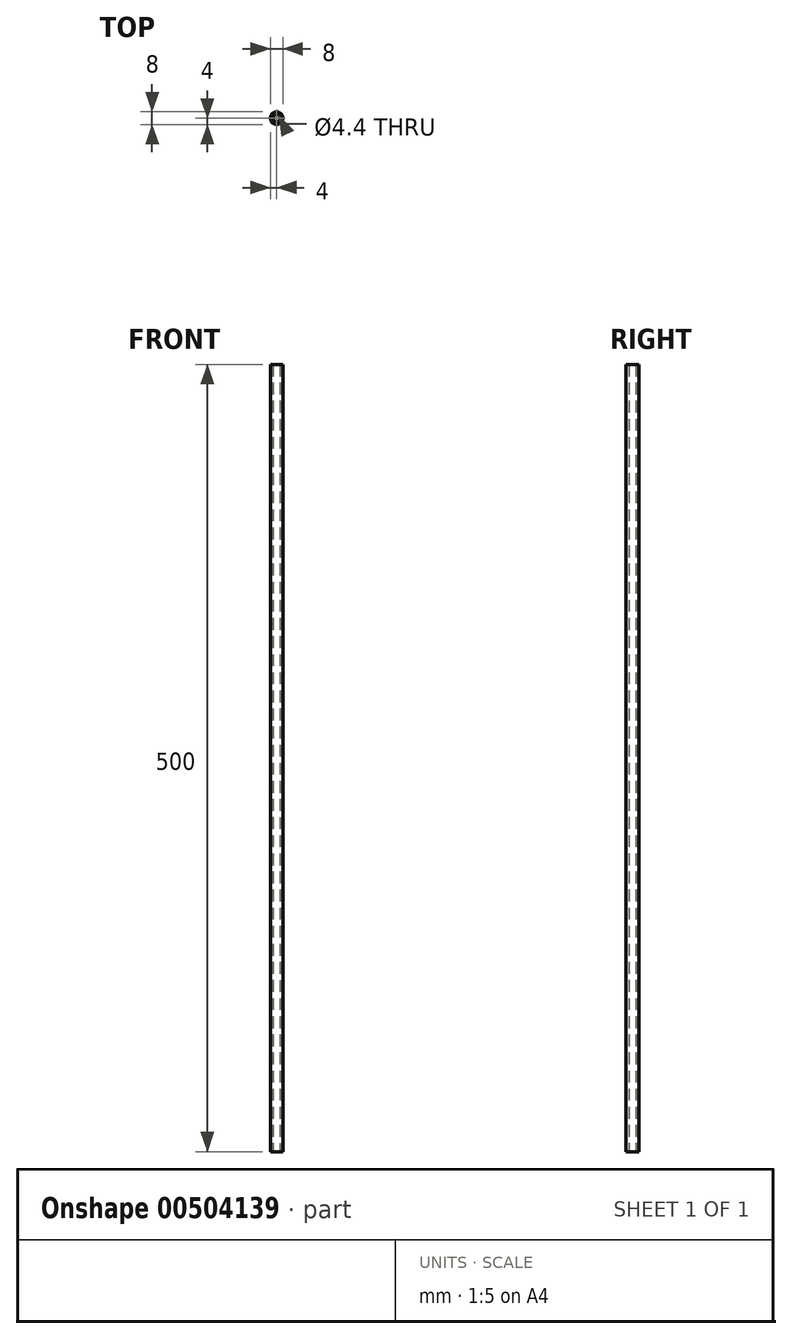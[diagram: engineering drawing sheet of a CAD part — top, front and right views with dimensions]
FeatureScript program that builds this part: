
annotation { "Feature Type Name" : "Feature", "Feature Type Description" : "" }
export const myFeature = defineFeature(function(context is Context, id is Id, definition is map)
    precondition{}
    {
        {
            var Q0;
            Q0=qCreatedBy(makeId("Top.planeOp"),FACE);
            var sketch = newSketch(context, id + "F0", { "sketchPlane" : qUnion([Q0])});
            skCircle(sketch, "E0", {"center": v(0, 0) * mm, "radius": 2.2 * mm});
            skCircle(sketch, "E1", {"center": v(0, 0) * mm, "radius": 4 * mm});
            skSolve(sketch);
        }
        {
            var Q0;
            Q0 = qSketchRegion(id + "F0", true);
            extrude(context, id + "F1", {"entities" : qUnion([Q0]), "depth" : 500 * mm, "offsetDistance" : 25 * mm});
        }
    });
